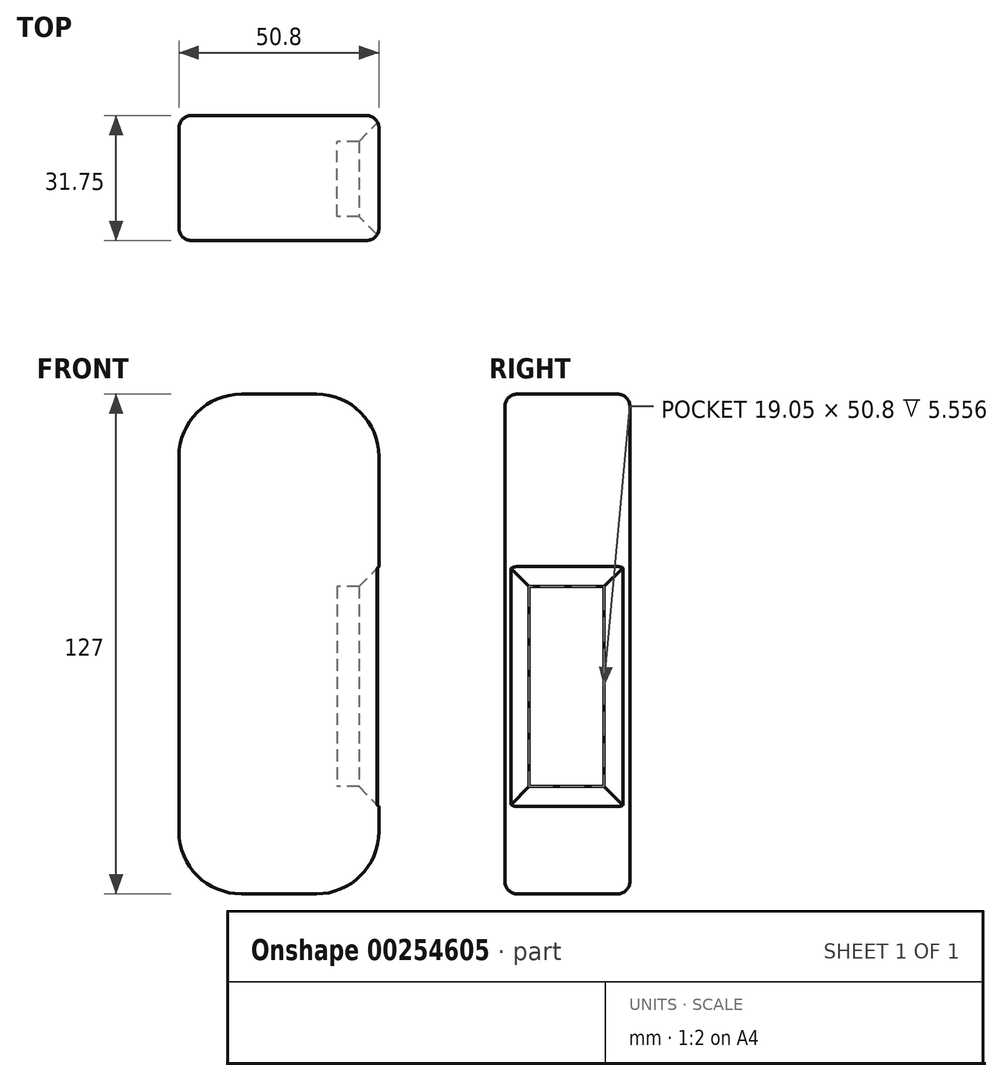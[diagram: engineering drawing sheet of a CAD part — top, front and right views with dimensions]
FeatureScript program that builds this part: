
annotation { "Feature Type Name" : "Feature", "Feature Type Description" : "" }
export const myFeature = defineFeature(function(context is Context, id is Id, definition is map)
    precondition{}
    {
        {
            var Q0;
            Q0=qCreatedBy(makeId("Front.planeOp"),FACE);
            var sketch = newSketch(context, id + "F0", { "sketchPlane" : qUnion([Q0])});
            skLineSegment(sketch, "E0.bottom", {"start": v(-24.29, 71.8) * mm, "end": v(-5.24, 71.8) * mm});
            skLineSegment(sketch, "E0.top", {"start": v(-24.29, -55.2) * mm, "end": v(-5.24, -55.2) * mm});
            skLineSegment(sketch, "E0.left", {"start": v(-40.16, 55.92) * mm, "end": v(-40.16, -39.33) * mm});
            skLineSegment(sketch, "E0.right", {"start": v(10.64, 55.92) * mm, "end": v(10.64, -39.33) * mm});
            skPoint(sketch, "E1.visualSharp", {"position": v(-40.16, 71.8) * mm});
            skArc(sketch, "E1.filletArc", {"start": v(-24.29, 71.8) * mm, "mid": v(-35.51, 67.15) * mm, "end": v(-40.16, 55.92) * mm});
            skPoint(sketch, "E2.visualSharp", {"position": v(10.64, 71.8) * mm});
            skArc(sketch, "E2.filletArc", {"start": v(10.64, 55.92) * mm, "mid": v(5.99, 67.15) * mm, "end": v(-5.24, 71.8) * mm});
            skPoint(sketch, "E3.visualSharp", {"position": v(10.64, -55.2) * mm});
            skArc(sketch, "E3.filletArc", {"start": v(-5.24, -55.2) * mm, "mid": v(5.99, -50.55) * mm, "end": v(10.64, -39.33) * mm});
            skPoint(sketch, "E4.visualSharp", {"position": v(-40.16, -55.2) * mm});
            skArc(sketch, "E4.filletArc", {"start": v(-40.16, -39.33) * mm, "mid": v(-35.51, -50.55) * mm, "end": v(-24.29, -55.2) * mm});
            skSolve(sketch);
        }
        {
            var Q0;
            Q0 = qSketchRegion(id + "F0", true);
            extrude(context, id + "F1", {"entities" : qUnion([Q0]), "depth" : 31.75 * mm});
        }
        {
            var Q0;
            Q0=makeQuery(id+"F1.opExtrude","SWEPT_FACE",FACE,{"disambiguationData":[OSD([sQuery(id+"F0.wireOp",EDGE,"E0.top")])]});
            var Q1;
            Q1=makeQuery(id+"F1.opExtrude","SWEPT_FACE",FACE,{"disambiguationData":[OSD([sQuery(id+"F0.wireOp",EDGE,"E0.bottom")])]});
            fillet(context, id + "F2", {"entities" : qUnion([Q0, Q1]), "radius" : 3.17 * mm, "tangentPropagation" : true, "allowEdgeOverflow" : false});
        }
        {
            var Q0;
            Q0=qCreatedBy(makeId("Right.planeOp"),FACE);
            var sketch = newSketch(context, id + "F3", { "sketchPlane" : qUnion([Q0])});
            skLineSegment(sketch, "E5.bottom", {"start": v(-25.63, 22.89) * mm, "end": v(-6.58, 22.89) * mm});
            skLineSegment(sketch, "E5.top", {"start": v(-25.63, -27.91) * mm, "end": v(-6.58, -27.91) * mm});
            skLineSegment(sketch, "E5.left", {"start": v(-25.63, 22.89) * mm, "end": v(-25.63, -27.91) * mm});
            skLineSegment(sketch, "E5.right", {"start": v(-6.58, 22.89) * mm, "end": v(-6.58, -27.91) * mm});
            skSolve(sketch);
        }
        {
            var Q0;
            Q0 = qSketchRegion(id + "F3", true);
            extrude(context, id + "F4", {"entities" : qUnion([Q0]), "operationType" : NewBodyOperationType.REMOVE, "endBound" : BoundingType.THROUGH_ALL, "depth" : 25.4 * mm});
        }
        {
            var Q0;
            Q0=makeQuery(id+"F4.boolean.opBoolean","INTERSECT",EDGE,{"derivedFrom":[makeQuery(id+"F1.opExtrude","SWEPT_FACE",FACE,{"disambiguationData":[OSD([sQuery(id+"F0.wireOp",EDGE,"E0.right")])]}),makeQuery(id+"F4.opExtrude","SWEPT_FACE",FACE,{"disambiguationData":[OSD([sQuery(id+"F3.wireOp",EDGE,"E5.left")])]})]});
            var Q1;
            Q1=makeQuery(id+"F4.boolean.opBoolean","INTERSECT",EDGE,{"derivedFrom":[makeQuery(id+"F1.opExtrude","SWEPT_FACE",FACE,{"disambiguationData":[OSD([sQuery(id+"F0.wireOp",EDGE,"E0.right")])]}),makeQuery(id+"F4.opExtrude","SWEPT_FACE",FACE,{"disambiguationData":[OSD([sQuery(id+"F3.wireOp",EDGE,"E5.bottom")])]})]});
            var Q2;
            Q2=makeQuery(id+"F4.boolean.opBoolean","INTERSECT",EDGE,{"derivedFrom":[makeQuery(id+"F1.opExtrude","SWEPT_FACE",FACE,{"disambiguationData":[OSD([sQuery(id+"F0.wireOp",EDGE,"E0.right")])]}),makeQuery(id+"F4.opExtrude","SWEPT_FACE",FACE,{"disambiguationData":[OSD([sQuery(id+"F3.wireOp",EDGE,"E5.top")])]})]});
            var Q3;
            Q3=makeQuery(id+"F4.boolean.opBoolean","INTERSECT",EDGE,{"derivedFrom":[makeQuery(id+"F1.opExtrude","SWEPT_FACE",FACE,{"disambiguationData":[OSD([sQuery(id+"F0.wireOp",EDGE,"E0.right")])]}),makeQuery(id+"F4.opExtrude","SWEPT_FACE",FACE,{"disambiguationData":[OSD([sQuery(id+"F3.wireOp",EDGE,"E5.right")])]})]});
            chamfer(context, id + "F5", {"entities" : qUnion([Q0, Q1, Q2, Q3]), "width" : 5.08 * mm, "tangentPropagation" : true});
        }
    });
